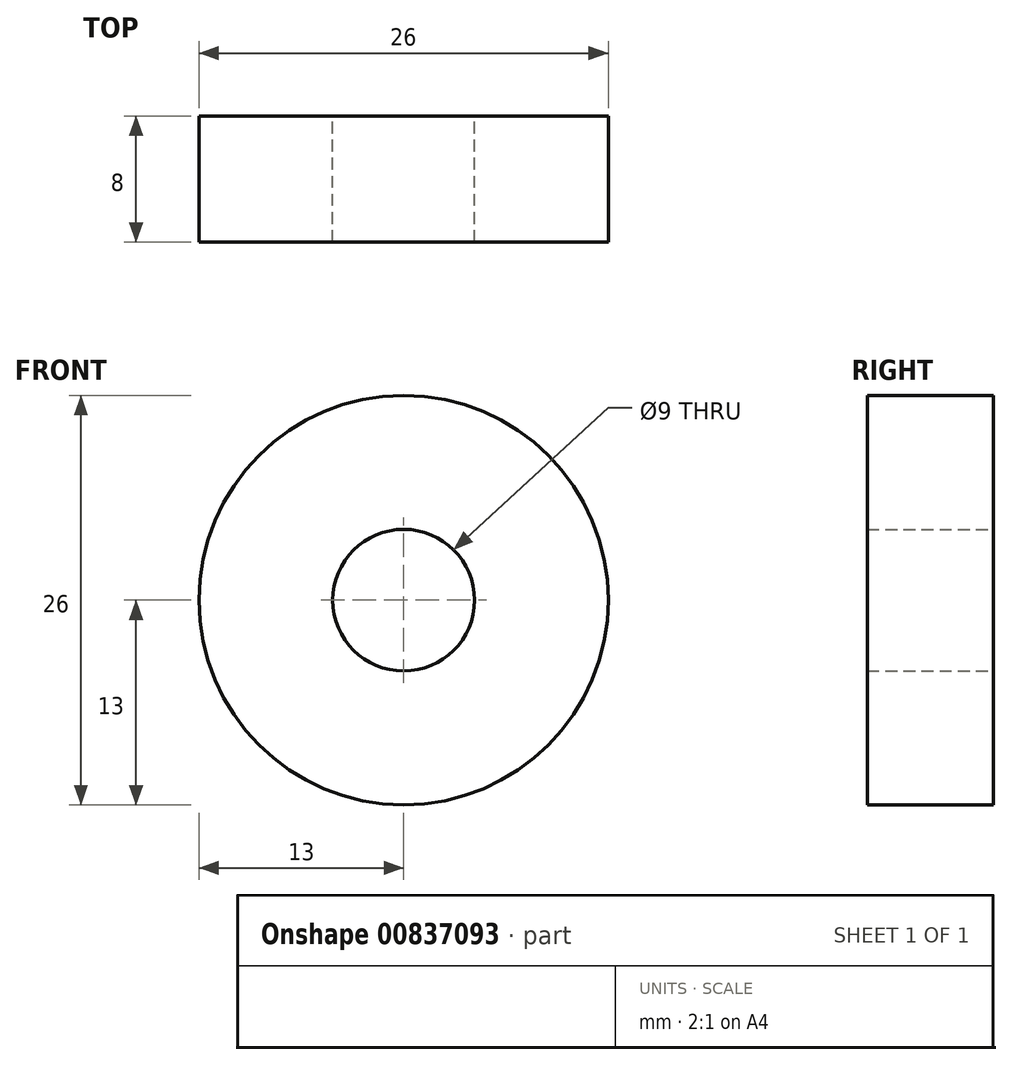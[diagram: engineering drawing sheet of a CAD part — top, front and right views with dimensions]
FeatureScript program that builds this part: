
annotation { "Feature Type Name" : "Feature", "Feature Type Description" : "" }
export const myFeature = defineFeature(function(context is Context, id is Id, definition is map)
    precondition{}
    {
        {
            var Q0;
            Q0=qCreatedBy(makeId("Front.planeOp"),FACE);
            var sketch = newSketch(context, id + "F0", { "sketchPlane" : qUnion([Q0])});
            skCircle(sketch, "E0", {"center": v(0, 0) * mm, "radius": 4.5 * mm});
            skCircle(sketch, "E1", {"center": v(0, 0) * mm, "radius": 13 * mm});
            skSolve(sketch);
        }
        {
            var Q0;
            Q0=makeQuery(id+"F0.imprint","IMPRINT",FACE,{"disambiguationData":[TD([[makeQuery(id+"F0.imprint","IMPRINT",EDGE,{"derivedFrom":sQuery(id+"F0.wireOp",EDGE,"E0")}),-1.0]])]});
            extrude(context, id + "F1", {"entities" : qUnion([Q0]), "depth" : 8 * mm, "offsetDistance" : 25 * mm});
        }
    });
